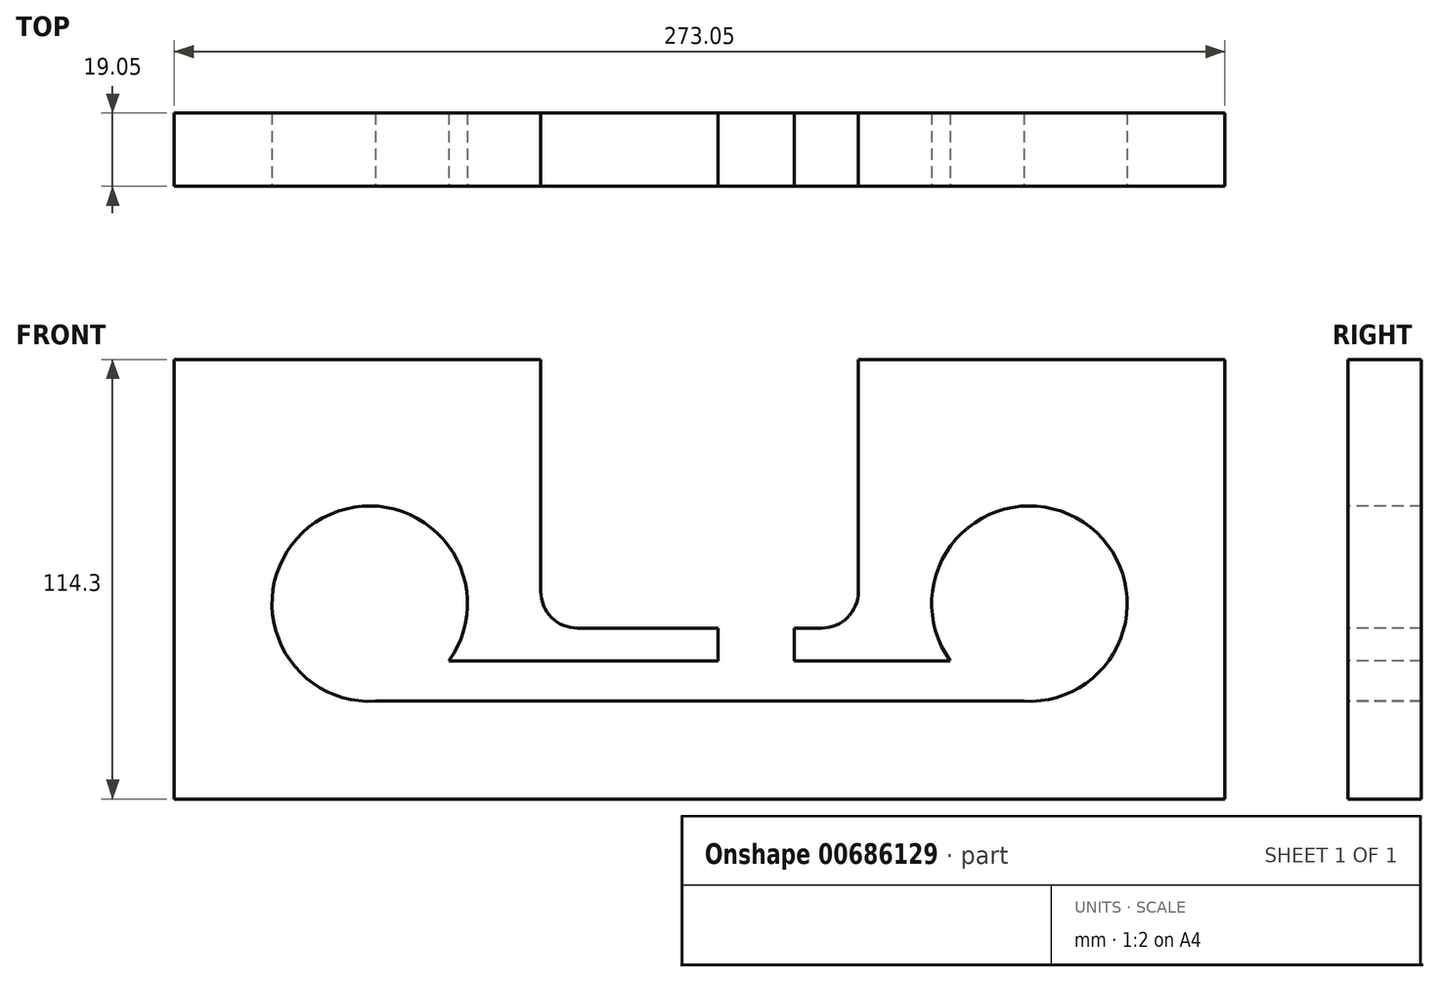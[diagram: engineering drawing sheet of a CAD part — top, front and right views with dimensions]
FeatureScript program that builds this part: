
annotation { "Feature Type Name" : "Feature", "Feature Type Description" : "" }
export const myFeature = defineFeature(function(context is Context, id is Id, definition is map)
    precondition{}
    {
        {
            var Q0;
            Q0=qCreatedBy(makeId("Front.planeOp"),FACE);
            var sketch = newSketch(context, id + "F0", { "sketchPlane" : qUnion([Q0])});
            skLineSegment(sketch, "E0.bottom", {"start": v(0, 0) * mm, "end": v(273.05, 0) * mm});
            skLineSegment(sketch, "E0.top", {"start": v(0, 114.3) * mm, "end": v(273.05, 114.3) * mm});
            skLineSegment(sketch, "E0.left", {"start": v(0, 0) * mm, "end": v(0, 114.3) * mm});
            skLineSegment(sketch, "E0.right", {"start": v(273.05, 0) * mm, "end": v(273.05, 114.3) * mm});
            skSolve(sketch);
        }
        {
            var Q0;
            Q0=makeQuery(id+"F0.imprint","IMPRINT",FACE,{"disambiguationData":[TD([[makeQuery(id+"F0.imprint","IMPRINT",EDGE,{"derivedFrom":sQuery(id+"F0.wireOp",EDGE,"E0.bottom")}),1.0]])]});
            extrude(context, id + "F1", {"entities" : qUnion([Q0]), "depth" : 19.05 * mm, "offsetDistance" : 25.4 * mm});
        }
        {
            var Q0;
            Q0=makeQuery(id+"F1.opExtrude","CAP_FACE",FACE,{"disambiguationData":[OSD([sQuery(id+"F0.wireOp",EDGE,"E0.bottom"),sQuery(id+"F0.wireOp",EDGE,"E0.top"),sQuery(id+"F0.wireOp",EDGE,"E0.left"),sQuery(id+"F0.wireOp",EDGE,"E0.right")])],"isStart":false});
            var sketch = newSketch(context, id + "F2", { "sketchPlane" : qUnion([Q0])});
            skCircle(sketch, "E1", {"center": v(50.8, 50.8) * mm, "radius": 25.4 * mm});
            skCircle(sketch, "E2", {"center": v(222.25, 50.8) * mm, "radius": 25.4 * mm});
            skSolve(sketch);
        }
        {
            var Q0;
            Q0=qSketchRegion(id+"F2",true);
            extrude(context, id + "F3", {"entities" : qUnion([Q0]), "operationType" : NewBodyOperationType.REMOVE, "oppositeDirection" : true, "depth" : 25.4 * mm, "offsetDistance" : 25.4 * mm});
        }
        {
            var Q0;
            Q0=makeQuery(id+"F1.opExtrude","CAP_FACE",FACE,{"disambiguationData":[OSD([sQuery(id+"F0.wireOp",EDGE,"E0.bottom"),sQuery(id+"F0.wireOp",EDGE,"E0.top"),sQuery(id+"F0.wireOp",EDGE,"E0.left"),sQuery(id+"F0.wireOp",EDGE,"E0.right")])],"isStart":false});
            var sketch = newSketch(context, id + "F4", { "sketchPlane" : qUnion([Q0])});
            skLineSegment(sketch, "E3", {"start": v(95.25, 114.3) * mm, "end": v(95.25, 53.97) * mm});
            skLineSegment(sketch, "E4", {"start": v(104.78, 44.45) * mm, "end": v(168.28, 44.45) * mm});
            skLineSegment(sketch, "E5", {"start": v(177.8, 53.97) * mm, "end": v(177.8, 114.3) * mm});
            skArc(sketch, "E6", {"start": v(95.25, 53.97) * mm, "mid": v(98.04, 47.24) * mm, "end": v(104.78, 44.45) * mm});
            skArc(sketch, "E7", {"start": v(168.28, 44.45) * mm, "mid": v(175.01, 47.24) * mm, "end": v(177.8, 53.97) * mm});
            skLineSegment(sketch, "E8", {"start": v(95.25, 114.3) * mm, "end": v(177.8, 114.3) * mm});
            skSolve(sketch);
        }
        {
            var Q0;
            Q0=makeQuery(id+"F4.imprint","IMPRINT",FACE,{"disambiguationData":[TD([[makeQuery(id+"F4.imprint","IMPRINT",EDGE,{"derivedFrom":sQuery(id+"F4.wireOp",EDGE,"E3")}),1.0]])]});
            extrude(context, id + "F5", {"entities" : qUnion([Q0]), "operationType" : NewBodyOperationType.REMOVE, "oppositeDirection" : true, "depth" : 25.4 * mm, "offsetDistance" : 25.4 * mm});
        }
        {
            var Q0;
            Q0=makeQuery(id+"F1.opExtrude","CAP_FACE",FACE,{"disambiguationData":[OSD([sQuery(id+"F0.wireOp",EDGE,"E0.bottom"),sQuery(id+"F0.wireOp",EDGE,"E0.top"),sQuery(id+"F0.wireOp",EDGE,"E0.left"),sQuery(id+"F0.wireOp",EDGE,"E0.right")])],"isStart":false});
            var sketch = newSketch(context, id + "F6", { "sketchPlane" : qUnion([Q0])});
            skLineSegment(sketch, "E9", {"start": v(49.34, 25.44) * mm, "end": v(223.71, 25.44) * mm});
            skLineSegment(sketch, "E10", {"start": v(71.37, 35.9) * mm, "end": v(141.38, 35.9) * mm});
            skLineSegment(sketch, "E11", {"start": v(71.37, 35.9) * mm, "end": v(49.34, 25.44) * mm});
            skLineSegment(sketch, "E12", {"start": v(201.68, 35.9) * mm, "end": v(223.71, 25.44) * mm});
            skLineSegment(sketch, "E13", {"start": v(141.38, 35.9) * mm, "end": v(141.38, 44.45) * mm});
            skLineSegment(sketch, "E14", {"start": v(141.38, 44.45) * mm, "end": v(161.07, 44.45) * mm});
            skLineSegment(sketch, "E15", {"start": v(161.07, 44.45) * mm, "end": v(161.07, 35.9) * mm});
            skLineSegment(sketch, "E16.trimOffspring", {"start": v(161.07, 35.9) * mm, "end": v(201.68, 35.9) * mm});
            skSolve(sketch);
        }
        {
            var Q0;
            Q0 = qSketchRegion(id + "F6", true);
            extrude(context, id + "F7", {"entities" : qUnion([Q0]), "operationType" : NewBodyOperationType.REMOVE, "oppositeDirection" : true, "depth" : 25.4 * mm, "offsetDistance" : 25.4 * mm});
        }
    });
